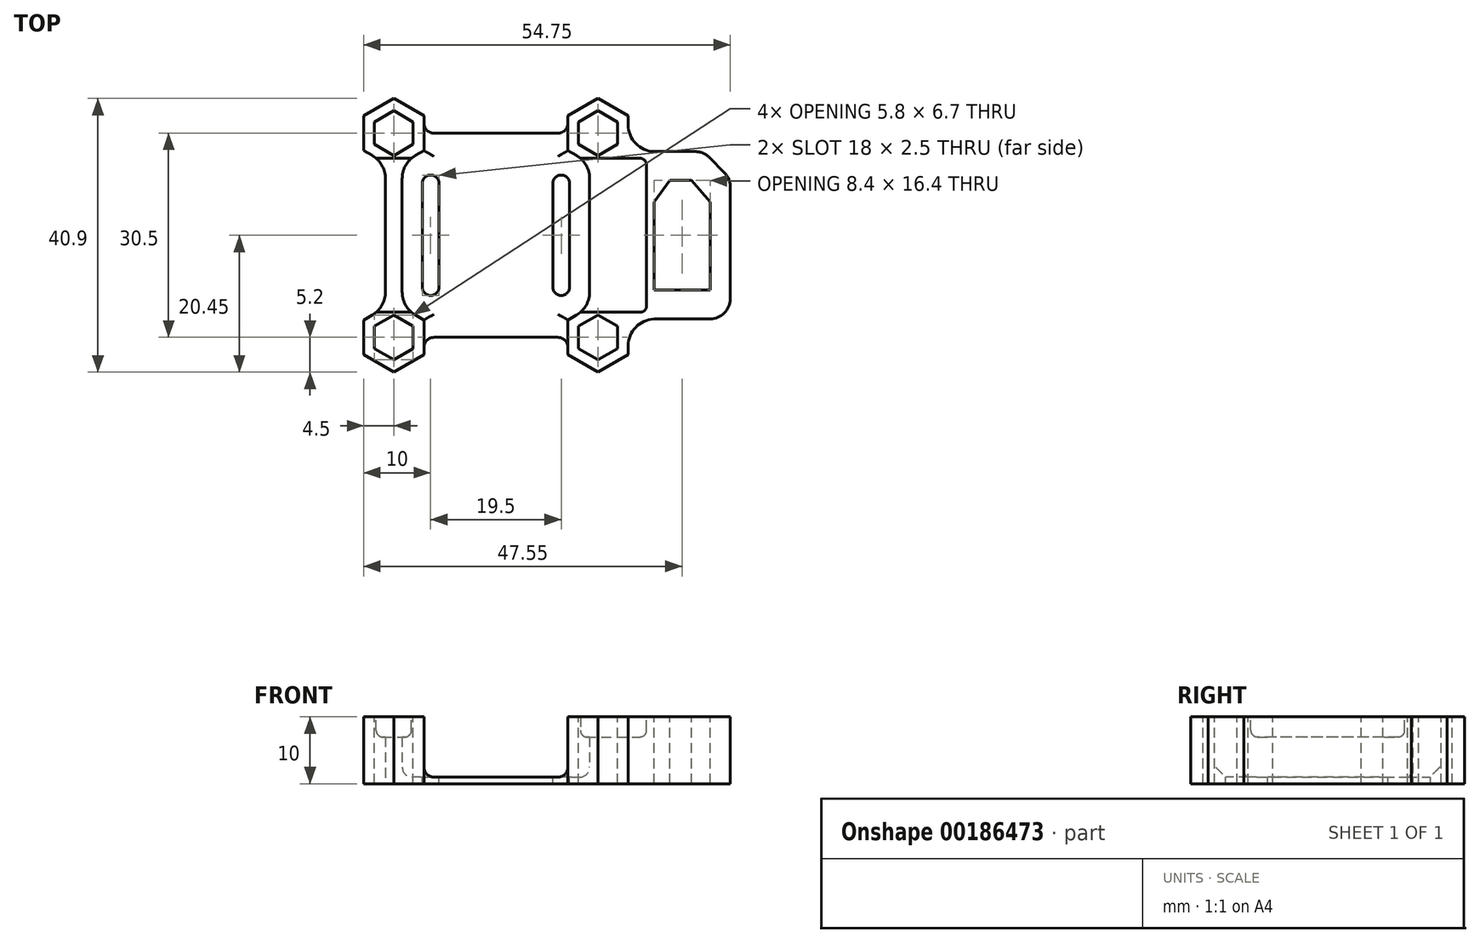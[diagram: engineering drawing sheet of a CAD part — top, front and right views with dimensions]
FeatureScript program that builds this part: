
annotation { "Feature Type Name" : "Feature", "Feature Type Description" : "" }
export const myFeature = defineFeature(function(context is Context, id is Id, definition is map)
    precondition{}
    {
        {
            var Q0;
            Q0=qCreatedBy(makeId("Top.planeOp"),FACE);
            var sketch = newSketch(context, id + "F0", { "sketchPlane" : qUnion([Q0])});
            skLineSegment(sketch, "E0.bottom", {"start": v(-15.25, 15.25) * mm, "end": v(15.25, 15.25) * mm});
            skLineSegment(sketch, "E0.top", {"start": v(-15.25, -15.25) * mm, "end": v(15.25, -15.25) * mm});
            skLineSegment(sketch, "E0.left", {"start": v(-15.25, 15.25) * mm, "end": v(-15.25, -15.25) * mm});
            skLineSegment(sketch, "E0.right", {"start": v(15.25, 15.25) * mm, "end": v(15.25, -15.25) * mm});
            skSolve(sketch);
        }
        {
            var Q0;
            Q0=qSketchRegion(id+"F0",true);
            extrude(context, id + "F1", {"entities" : qUnion([Q0]), "depth" : 1 * mm});
        }
        {
            var Q0;
            Q0=qCreatedBy(makeId("Top.planeOp"),FACE);
            var sketch = newSketch(context, id + "F2", { "sketchPlane" : qUnion([Q0])});
            skCircle(sketch, "E1.cCircle", {"center": v(-15.25, 15.25) * mm, "radius": 4.5 * mm, "construction": true});
            skLineSegment(sketch, "E1.0", {"start": v(-16.5, 10.78) * mm, "end": v(-19.75, 12.65) * mm});
            skLineSegment(sketch, "E1.1", {"start": v(-19.75, 12.65) * mm, "end": v(-19.75, 17.85) * mm});
            skLineSegment(sketch, "E1.2", {"start": v(-19.75, 17.85) * mm, "end": v(-15.25, 20.45) * mm});
            skLineSegment(sketch, "E1.3", {"start": v(-15.25, 20.45) * mm, "end": v(-10.75, 17.85) * mm});
            skLineSegment(sketch, "E1.4", {"start": v(-10.75, 17.85) * mm, "end": v(-10.75, 12.65) * mm});
            skLineSegment(sketch, "E1.5", {"start": v(-10.75, 12.65) * mm, "end": v(-14, 10.78) * mm});
            skPoint(sketch, "E1.0.midPoint", {"position": v(-17.5, 11.35) * mm});
            skCircle(sketch, "E2.MirrorC", {"center": v(15.25, 15.25) * mm, "radius": 4.5 * mm, "construction": true});
            skLineSegment(sketch, "E3.MirrorCS", {"start": v(19.75, 12.65) * mm, "end": v(19.75, 17.85) * mm});
            skLineSegment(sketch, "E4.MirrorCS", {"start": v(19.75, 17.85) * mm, "end": v(15.25, 20.45) * mm});
            skLineSegment(sketch, "E5.MirrorCS", {"start": v(15.25, 20.45) * mm, "end": v(10.75, 17.85) * mm});
            skLineSegment(sketch, "E6.MirrorCS", {"start": v(10.75, 17.85) * mm, "end": v(10.75, 12.65) * mm});
            skLineSegment(sketch, "E7.MirrorCS", {"start": v(10.75, 12.65) * mm, "end": v(14, 10.78) * mm});
            skPoint(sketch, "E8.MirrorP", {"position": v(17.5, 11.35) * mm});
            skLineSegment(sketch, "E9.MirrorCS", {"start": v(-16.5, -10.78) * mm, "end": v(-19.75, -12.65) * mm});
            skLineSegment(sketch, "E10.MirrorCS", {"start": v(-19.75, -12.65) * mm, "end": v(-19.75, -17.85) * mm});
            skLineSegment(sketch, "E11.MirrorCS", {"start": v(10.75, -17.85) * mm, "end": v(10.75, -12.65) * mm});
            skLineSegment(sketch, "E12.MirrorCS", {"start": v(10.75, -12.65) * mm, "end": v(14, -10.78) * mm});
            skLineSegment(sketch, "E13.MirrorCS", {"start": v(-19.75, -17.85) * mm, "end": v(-15.25, -20.45) * mm});
            skLineSegment(sketch, "E14.MirrorCS", {"start": v(15.25, -20.45) * mm, "end": v(10.75, -17.85) * mm});
            skLineSegment(sketch, "E15.MirrorCS", {"start": v(-15.25, -20.45) * mm, "end": v(-10.75, -17.85) * mm});
            skLineSegment(sketch, "E16.MirrorCS", {"start": v(19.75, -17.85) * mm, "end": v(15.25, -20.45) * mm});
            skLineSegment(sketch, "E17.MirrorCS", {"start": v(-10.75, -17.85) * mm, "end": v(-10.75, -12.65) * mm});
            skLineSegment(sketch, "E18.MirrorCS", {"start": v(19.75, -12.65) * mm, "end": v(19.75, -17.85) * mm});
            skCircle(sketch, "E19.MirrorC", {"center": v(-15.25, -15.25) * mm, "radius": 4.5 * mm, "construction": true});
            skCircle(sketch, "E20.MirrorC", {"center": v(15.25, -15.25) * mm, "radius": 4.5 * mm, "construction": true});
            skPoint(sketch, "E21.MirrorP", {"position": v(17.5, -11.35) * mm});
            skLineSegment(sketch, "E22.MirrorCS", {"start": v(-10.75, -12.65) * mm, "end": v(-14, -10.78) * mm});
            skPoint(sketch, "E23.MirrorP", {"position": v(-17.5, -11.35) * mm});
            skLineSegment(sketch, "E24", {"start": v(-16.5, 10.78) * mm, "end": v(-16.5, -10.78) * mm});
            skLineSegment(sketch, "E25", {"start": v(-14, -10.78) * mm, "end": v(-14, 10.78) * mm});
            skLineSegment(sketch, "E26", {"start": v(14, 10.78) * mm, "end": v(14, -10.78) * mm});
            skPoint(sketch, "E27.orphan", {"position": v(-15.25, 10.05) * mm});
            skPoint(sketch, "E28.orphan", {"position": v(-15.25, -10.05) * mm});
            skPoint(sketch, "E29.orphan", {"position": v(15.25, -10.05) * mm});
            skPoint(sketch, "E30.orphan", {"position": v(15.25, 10.05) * mm});
            skLineSegment(sketch, "E31", {"start": v(24, 12.5) * mm, "end": v(24, -12.5) * mm, "construction": true});
            skLineSegment(sketch, "E32", {"start": v(24, -12.5) * mm, "end": v(19.75, -12.65) * mm});
            skLineSegment(sketch, "E33", {"start": v(24, 12.5) * mm, "end": v(19.75, 12.65) * mm});
            skLineSegment(sketch, "E34.bottom", {"start": v(24, 12.5) * mm, "end": v(35, 12.5) * mm});
            skLineSegment(sketch, "E34.top", {"start": v(24, -12.5) * mm, "end": v(35, -12.5) * mm});
            skLineSegment(sketch, "E34.right", {"start": v(35, 12.5) * mm, "end": v(35, -12.5) * mm});
            skSolve(sketch);
        }
        {
            var Q0;
            Q0=qSketchRegion(id+"F2",true);
            extrude(context, id + "F3", {"entities" : qUnion([Q0]), "operationType" : NewBodyOperationType.ADD, "depth" : 10 * mm});
        }
        {
            var Q0;
            Q0=makeQuery(id+"F3.opExtrude","CAP_FACE",FACE,{"disambiguationData":[OSD([sQuery(id+"F2.wireOp",EDGE,"E3.MirrorCS"),sQuery(id+"F2.wireOp",EDGE,"E4.MirrorCS"),sQuery(id+"F2.wireOp",EDGE,"E5.MirrorCS"),sQuery(id+"F2.wireOp",EDGE,"E6.MirrorCS"),sQuery(id+"F2.wireOp",EDGE,"E7.MirrorCS"),sQuery(id+"F2.wireOp",EDGE,"E11.MirrorCS"),sQuery(id+"F2.wireOp",EDGE,"E12.MirrorCS"),sQuery(id+"F2.wireOp",EDGE,"E14.MirrorCS"),sQuery(id+"F2.wireOp",EDGE,"E16.MirrorCS"),sQuery(id+"F2.wireOp",EDGE,"E18.MirrorCS"),sQuery(id+"F2.wireOp",EDGE,"E26"),sQuery(id+"F2.wireOp",EDGE,"E31"),sQuery(id+"F2.wireOp",EDGE,"E32"),sQuery(id+"F2.wireOp",EDGE,"E33")])],"isStart":false});
            var sketch = newSketch(context, id + "F4", { "sketchPlane" : qUnion([Q0])});
            skLineSegment(sketch, "E35.bottom", {"start": v(-22.5, 11.5) * mm, "end": v(22.5, 11.5) * mm});
            skLineSegment(sketch, "E35.top", {"start": v(-22.5, -11.5) * mm, "end": v(22.5, -11.5) * mm});
            skLineSegment(sketch, "E35.left", {"start": v(-22.5, 11.5) * mm, "end": v(-22.5, -11.5) * mm});
            skLineSegment(sketch, "E35.right", {"start": v(22.5, 11.5) * mm, "end": v(22.5, -11.5) * mm});
            skPoint(sketch, "E36.visualSharp", {"position": v(22.5, 11.5) * mm});
            skPoint(sketch, "E37.visualSharp", {"position": v(22.5, -11.5) * mm});
            skSolve(sketch);
        }
        {
            var Q0;
            Q0=qSketchRegion(id+"F4",true);
            extrude(context, id + "F5", {"entities" : qUnion([Q0]), "operationType" : NewBodyOperationType.REMOVE, "oppositeDirection" : true, "depth" : 3 * mm});
        }
        {
            var Q0;
            {var subQ0=sQuery(id+"F2.wireOp",EDGE,"E34.top");var subQ1=sQuery(id+"F2.wireOp",EDGE,"E34.bottom");var subQ2=sQuery(id+"F2.wireOp",EDGE,"E33");var subQ3=sQuery(id+"F2.wireOp",EDGE,"E32");var subQ4=sQuery(id+"F2.wireOp",EDGE,"E34.right");Q0=makeQuery(id+"F5.boolean.opBoolean","SPLIT",FACE,{"disambiguationData":[TD([makeQuery(id+"F3.opExtrude","SWEPT_FACE",FACE,{"disambiguationData":[OSD([subQ3])]})])],"derivedFrom":makeQuery(id+"F3.opExtrude","CAP_FACE",FACE,{"disambiguationData":[OSD([sQuery(id+"F2.wireOp",EDGE,"E3.MirrorCS"),sQuery(id+"F2.wireOp",EDGE,"E4.MirrorCS"),sQuery(id+"F2.wireOp",EDGE,"E5.MirrorCS"),sQuery(id+"F2.wireOp",EDGE,"E6.MirrorCS"),sQuery(id+"F2.wireOp",EDGE,"E7.MirrorCS"),sQuery(id+"F2.wireOp",EDGE,"E11.MirrorCS"),sQuery(id+"F2.wireOp",EDGE,"E12.MirrorCS"),sQuery(id+"F2.wireOp",EDGE,"E14.MirrorCS"),sQuery(id+"F2.wireOp",EDGE,"E16.MirrorCS"),sQuery(id+"F2.wireOp",EDGE,"E18.MirrorCS"),sQuery(id+"F2.wireOp",EDGE,"E26"),subQ3,subQ2,subQ1,subQ0,subQ4])],"isStart":false})});}
            var sketch = newSketch(context, id + "F6", { "sketchPlane" : qUnion([Q0])});
            skLineSegment(sketch, "E38.bottom", {"start": v(26, 8.2) * mm, "end": v(29.2, 8.2) * mm});
            skLineSegment(sketch, "E38.top", {"start": v(23.6, -8.2) * mm, "end": v(32, -8.2) * mm});
            skLineSegment(sketch, "E38.left", {"start": v(23.6, 5) * mm, "end": v(23.6, -8.2) * mm});
            skLineSegment(sketch, "E38.right", {"start": v(32, 5) * mm, "end": v(32, -8.2) * mm});
            skLineSegment(sketch, "E39", {"start": v(26, 8.2) * mm, "end": v(23.6, 5) * mm});
            skLineSegment(sketch, "E40", {"start": v(29.2, 8.2) * mm, "end": v(32, 5) * mm});
            skCircle(sketch, "E41.cCircle", {"center": v(-15.25, 15.25) * mm, "radius": 2.9 * mm, "construction": true});
            skLineSegment(sketch, "E41.0", {"start": v(-12.35, 13.58) * mm, "end": v(-15.25, 11.9) * mm});
            skLineSegment(sketch, "E41.1", {"start": v(-15.25, 11.9) * mm, "end": v(-18.15, 13.58) * mm});
            skLineSegment(sketch, "E41.2", {"start": v(-18.15, 13.58) * mm, "end": v(-18.15, 16.92) * mm});
            skLineSegment(sketch, "E41.3", {"start": v(-18.15, 16.92) * mm, "end": v(-15.25, 18.6) * mm});
            skLineSegment(sketch, "E41.4", {"start": v(-15.25, 18.6) * mm, "end": v(-12.35, 16.92) * mm});
            skLineSegment(sketch, "E41.5", {"start": v(-12.35, 16.92) * mm, "end": v(-12.35, 13.58) * mm});
            skPoint(sketch, "E41.0.midPoint", {"position": v(-13.8, 12.74) * mm});
            skLineSegment(sketch, "E42.0.1.0", {"start": v(-15.25, -11.9) * mm, "end": v(-12.35, -13.58) * mm});
            skLineSegment(sketch, "E42.0.1.1", {"start": v(-15.25, -18.6) * mm, "end": v(-18.15, -16.92) * mm});
            skLineSegment(sketch, "E42.0.1.2", {"start": v(-18.15, -13.58) * mm, "end": v(-15.25, -11.9) * mm});
            skPoint(sketch, "E42.0.1.3", {"position": v(-13.8, -17.76) * mm});
            skCircle(sketch, "E42.0.1.4", {"center": v(-15.25, -15.25) * mm, "radius": 2.9 * mm, "construction": true});
            skLineSegment(sketch, "E42.0.1.5", {"start": v(-12.35, -13.58) * mm, "end": v(-12.35, -16.92) * mm});
            skLineSegment(sketch, "E42.0.1.6", {"start": v(-18.15, -16.92) * mm, "end": v(-18.15, -13.58) * mm});
            skLineSegment(sketch, "E42.0.1.7", {"start": v(-12.35, -16.92) * mm, "end": v(-15.25, -18.6) * mm});
            skLineSegment(sketch, "E42.direction1", {"start": v(-18.15, 13.58) * mm, "end": v(12.35, 13.58) * mm, "construction": true});
            skLineSegment(sketch, "E42.direction2", {"start": v(-18.15, 13.58) * mm, "end": v(-18.15, -16.92) * mm, "construction": true});
            skLineSegment(sketch, "E43.MirrorCS", {"start": v(12.35, 16.92) * mm, "end": v(12.35, 13.58) * mm});
            skLineSegment(sketch, "E44.MirrorCS", {"start": v(18.15, 16.92) * mm, "end": v(15.25, 18.6) * mm});
            skLineSegment(sketch, "E45.MirrorCS", {"start": v(12.35, -16.92) * mm, "end": v(15.25, -18.6) * mm});
            skLineSegment(sketch, "E46.MirrorCS", {"start": v(18.15, 13.58) * mm, "end": v(18.15, 16.92) * mm});
            skLineSegment(sketch, "E47.MirrorCS", {"start": v(15.25, 11.9) * mm, "end": v(18.15, 13.58) * mm});
            skLineSegment(sketch, "E48.MirrorCS", {"start": v(12.35, 13.58) * mm, "end": v(15.25, 11.9) * mm});
            skLineSegment(sketch, "E49.MirrorCS", {"start": v(18.15, -13.58) * mm, "end": v(15.25, -11.9) * mm});
            skLineSegment(sketch, "E50.MirrorCS", {"start": v(15.25, -11.9) * mm, "end": v(12.35, -13.58) * mm});
            skLineSegment(sketch, "E51.MirrorCS", {"start": v(12.35, -13.58) * mm, "end": v(12.35, -16.92) * mm});
            skLineSegment(sketch, "E52.MirrorCS", {"start": v(18.15, -16.92) * mm, "end": v(18.15, -13.58) * mm});
            skLineSegment(sketch, "E53.MirrorCS", {"start": v(15.25, 18.6) * mm, "end": v(12.35, 16.92) * mm});
            skCircle(sketch, "E54.MirrorC", {"center": v(15.25, -15.25) * mm, "radius": 2.9 * mm, "construction": true});
            skLineSegment(sketch, "E55.MirrorCS", {"start": v(15.25, -18.6) * mm, "end": v(18.15, -16.92) * mm});
            skPoint(sketch, "E56.MirrorP", {"position": v(13.8, -17.76) * mm});
            skLineSegment(sketch, "E57.MirrorCS", {"start": v(18.15, 13.58) * mm, "end": v(18.15, -16.92) * mm, "construction": true});
            skPoint(sketch, "E58.MirrorP", {"position": v(13.8, 12.74) * mm});
            skCircle(sketch, "E59.MirrorC", {"center": v(15.25, 15.25) * mm, "radius": 2.9 * mm, "construction": true});
            skSolve(sketch);
        }
        {
            var Q0;
            Q0=qSketchRegion(id+"F6",true);
            extrude(context, id + "F7", {"entities" : qUnion([Q0]), "operationType" : NewBodyOperationType.REMOVE, "endBound" : BoundingType.THROUGH_ALL, "oppositeDirection" : true, "depth" : 25 * mm});
        }
        {
            var Q0;
            Q0=makeQuery(id+"F3.opExtrude","SWEPT_EDGE",EDGE,{"disambiguationData":[OSD([sQuery(id+"F2.wireOp",EDGE,"E34.bottom"),sQuery(id+"F2.wireOp",EDGE,"E34.right")])]});
            chamfer(context, id + "F8", {"entities" : qUnion([Q0]), "width" : 4 * mm, "tangentPropagation" : true});
        }
        {
            var Q0;
            Q0=makeQuery(id+"F3.opExtrude","SWEPT_EDGE",EDGE,{"disambiguationData":[OSD([sQuery(id+"F2.wireOp",EDGE,"E1.0"),sQuery(id+"F2.wireOp",EDGE,"E24")])]});
            var Q1;
            Q1=makeQuery(id+"F3.opExtrude","SWEPT_EDGE",EDGE,{"disambiguationData":[OSD([sQuery(id+"F2.wireOp",EDGE,"E9.MirrorCS"),sQuery(id+"F2.wireOp",EDGE,"E24")])]});
            var Q2;
            Q2=makeQuery(id+"F3.opExtrude","SWEPT_EDGE",EDGE,{"disambiguationData":[OSD([sQuery(id+"F2.wireOp",EDGE,"E1.5"),sQuery(id+"F2.wireOp",EDGE,"E25")])]});
            var Q3;
            Q3=makeQuery(id+"F3.opExtrude","SWEPT_EDGE",EDGE,{"disambiguationData":[OSD([sQuery(id+"F2.wireOp",EDGE,"E22.MirrorCS"),sQuery(id+"F2.wireOp",EDGE,"E25")])]});
            var Q4;
            Q4=makeQuery(id+"F3.opExtrude","SWEPT_EDGE",EDGE,{"disambiguationData":[OSD([sQuery(id+"F2.wireOp",EDGE,"E7.MirrorCS"),sQuery(id+"F2.wireOp",EDGE,"E26")])]});
            var Q5;
            Q5=makeQuery(id+"F3.opExtrude","SWEPT_EDGE",EDGE,{"disambiguationData":[OSD([sQuery(id+"F2.wireOp",EDGE,"E12.MirrorCS"),sQuery(id+"F2.wireOp",EDGE,"E26")])]});
            var Q6;
            Q6=makeQuery(id+"F3.opExtrude","SWEPT_EDGE",EDGE,{"disambiguationData":[OSD([sQuery(id+"F2.wireOp",EDGE,"E33"),sQuery(id+"F2.wireOp",EDGE,"E34.bottom")])]});
            var Q7;
            Q7=makeQuery(id+"F3.opExtrude","SWEPT_EDGE",EDGE,{"disambiguationData":[OSD([sQuery(id+"F2.wireOp",EDGE,"E3.MirrorCS"),sQuery(id+"F2.wireOp",EDGE,"E33")])]});
            var Q8;
            Q8=makeQuery(id+"F3.opExtrude","SWEPT_EDGE",EDGE,{"disambiguationData":[OSD([sQuery(id+"F2.wireOp",EDGE,"E18.MirrorCS"),sQuery(id+"F2.wireOp",EDGE,"E32")])]});
            var Q9;
            Q9=makeQuery(id+"F3.opExtrude","SWEPT_EDGE",EDGE,{"disambiguationData":[OSD([sQuery(id+"F2.wireOp",EDGE,"E32"),sQuery(id+"F2.wireOp",EDGE,"E34.top")])]});
            fillet(context, id + "F9", {"entities" : qUnion([Q0, Q1, Q2, Q3, Q4, Q5, Q6, Q7, Q8, Q9]), "radius" : 4 * mm, "tangentPropagation" : true, "allowEdgeOverflow" : false});
        }
        {
            var Q0;
            {var subQ0=sQuery(id+"F4.wireOp",EDGE,"E35.top");Q0=makeQuery(id+"F5.boolean.opBoolean","COPY",EDGE,{"disambiguationData":[TD([makeQuery(id+"F3.opExtrude","SWEPT_FACE",FACE,{"disambiguationData":[OSD([sQuery(id+"F2.wireOp",EDGE,"E9.MirrorCS")])]})])],"derivedFrom":makeQuery(id+"F5.opExtrude","CAP_EDGE",EDGE,{"disambiguationData":[OSD([subQ0])],"isStart":false})});}
            var Q1;
            {var subQ0=sQuery(id+"F4.wireOp",EDGE,"E35.bottom");Q1=makeQuery(id+"F5.boolean.opBoolean","COPY",EDGE,{"disambiguationData":[TD([makeQuery(id+"F3.opExtrude","SWEPT_FACE",FACE,{"disambiguationData":[OSD([sQuery(id+"F2.wireOp",EDGE,"E1.0")])]})])],"derivedFrom":makeQuery(id+"F5.opExtrude","CAP_EDGE",EDGE,{"disambiguationData":[OSD([subQ0])],"isStart":false})});}
            var Q2;
            {var subQ1=sQuery(id+"F4.wireOp",EDGE,"E35.bottom");Q2=makeQuery(id+"F5.boolean.opBoolean","COPY",EDGE,{"disambiguationData":[TD([makeQuery(id+"F3.opExtrude","SWEPT_FACE",FACE,{"disambiguationData":[OSD([sQuery(id+"F2.wireOp",EDGE,"E3.MirrorCS")])]})])],"derivedFrom":makeQuery(id+"F5.opExtrude","CAP_EDGE",EDGE,{"disambiguationData":[OSD([subQ1])],"isStart":false})});}
            var Q3;
            {var subQ0=sQuery(id+"F4.wireOp",EDGE,"E35.top");Q3=makeQuery(id+"F5.boolean.opBoolean","COPY",EDGE,{"disambiguationData":[TD([makeQuery(id+"F3.opExtrude","SWEPT_FACE",FACE,{"disambiguationData":[OSD([sQuery(id+"F2.wireOp",EDGE,"E12.MirrorCS")])]})])],"derivedFrom":makeQuery(id+"F5.opExtrude","CAP_EDGE",EDGE,{"disambiguationData":[OSD([subQ0])],"isStart":false})});}
            var Q4;
            Q4=makeQuery(id+"F5.boolean.opBoolean","COPY",EDGE,{"derivedFrom":makeQuery(id+"F5.opExtrude","CAP_EDGE",EDGE,{"disambiguationData":[OSD([sQuery(id+"F4.wireOp",EDGE,"E35.right")])],"isStart":false})});
            var Q5;
            {var subQ0=sQuery(id+"F4.wireOp",EDGE,"E35.bottom");Q5=makeQuery(id+"F5.boolean.opBoolean","COPY",EDGE,{"disambiguationData":[TD([makeQuery(id+"F3.opExtrude","SWEPT_FACE",FACE,{"disambiguationData":[OSD([sQuery(id+"F2.wireOp",EDGE,"E7.MirrorCS")])]})])],"derivedFrom":makeQuery(id+"F5.opExtrude","CAP_EDGE",EDGE,{"disambiguationData":[OSD([subQ0])],"isStart":false})});}
            fillet(context, id + "F10", {"entities" : qUnion([Q0, Q1, Q2, Q3, Q4, Q5]), "radius" : 1 * mm, "tangentPropagation" : true, "allowEdgeOverflow" : false});
        }
        {
            var Q0;
            Q0=makeQuery(id+"F9.opFillet","BLEND_EDGE",EDGE,{"blendedFrom":[makeQuery(id+"F3.opExtrude","SWEPT_EDGE",EDGE,{"disambiguationData":[OSD([sQuery(id+"F2.wireOp",EDGE,"E22.MirrorCS"),sQuery(id+"F2.wireOp",EDGE,"E25")])]}),makeQuery(id+"F1.opExtrude","CAP_FACE",FACE,{"disambiguationData":[OSD([sQuery(id+"F0.wireOp",EDGE,"E0.bottom"),sQuery(id+"F0.wireOp",EDGE,"E0.top"),sQuery(id+"F0.wireOp",EDGE,"E0.left"),sQuery(id+"F0.wireOp",EDGE,"E0.right")])],"isStart":false})],"blendedInto":[makeQuery(id+"F1.opExtrude","CAP_FACE",FACE,{"disambiguationData":[OSD([sQuery(id+"F0.wireOp",EDGE,"E0.bottom"),sQuery(id+"F0.wireOp",EDGE,"E0.top"),sQuery(id+"F0.wireOp",EDGE,"E0.left"),sQuery(id+"F0.wireOp",EDGE,"E0.right")])],"isStart":false})]});
            var Q1;
            Q1=makeQuery(id+"F3.boolean.opBoolean","INTERSECT",EDGE,{"derivedFrom":[makeQuery(id+"F1.opExtrude","CAP_FACE",FACE,{"disambiguationData":[OSD([sQuery(id+"F0.wireOp",EDGE,"E0.bottom"),sQuery(id+"F0.wireOp",EDGE,"E0.top"),sQuery(id+"F0.wireOp",EDGE,"E0.left"),sQuery(id+"F0.wireOp",EDGE,"E0.right")])],"isStart":false}),makeQuery(id+"F3.opExtrude","SWEPT_FACE",FACE,{"disambiguationData":[OSD([sQuery(id+"F2.wireOp",EDGE,"E17.MirrorCS")])]})]});
            var Q2;
            Q2=makeQuery(id+"F3.boolean.opBoolean","INTERSECT",EDGE,{"derivedFrom":[makeQuery(id+"F1.opExtrude","CAP_FACE",FACE,{"disambiguationData":[OSD([sQuery(id+"F0.wireOp",EDGE,"E0.bottom"),sQuery(id+"F0.wireOp",EDGE,"E0.top"),sQuery(id+"F0.wireOp",EDGE,"E0.left"),sQuery(id+"F0.wireOp",EDGE,"E0.right")])],"isStart":false}),makeQuery(id+"F3.opExtrude","SWEPT_FACE",FACE,{"disambiguationData":[OSD([sQuery(id+"F2.wireOp",EDGE,"E1.4")])]})]});
            var Q3;
            Q3=makeQuery(id+"F3.boolean.opBoolean","INTERSECT",EDGE,{"derivedFrom":[makeQuery(id+"F1.opExtrude","CAP_FACE",FACE,{"disambiguationData":[OSD([sQuery(id+"F0.wireOp",EDGE,"E0.bottom"),sQuery(id+"F0.wireOp",EDGE,"E0.top"),sQuery(id+"F0.wireOp",EDGE,"E0.left"),sQuery(id+"F0.wireOp",EDGE,"E0.right")])],"isStart":false}),makeQuery(id+"F3.opExtrude","SWEPT_FACE",FACE,{"disambiguationData":[OSD([sQuery(id+"F2.wireOp",EDGE,"E26")])]})]});
            var Q4;
            Q4=makeQuery(id+"F3.boolean.opBoolean","INTERSECT",EDGE,{"derivedFrom":[makeQuery(id+"F1.opExtrude","CAP_FACE",FACE,{"disambiguationData":[OSD([sQuery(id+"F0.wireOp",EDGE,"E0.bottom"),sQuery(id+"F0.wireOp",EDGE,"E0.top"),sQuery(id+"F0.wireOp",EDGE,"E0.left"),sQuery(id+"F0.wireOp",EDGE,"E0.right")])],"isStart":false}),makeQuery(id+"F3.opExtrude","SWEPT_FACE",FACE,{"disambiguationData":[OSD([sQuery(id+"F2.wireOp",EDGE,"E6.MirrorCS")])]})]});
            var Q5;
            Q5=makeQuery(id+"F3.boolean.opBoolean","INTERSECT",EDGE,{"derivedFrom":[makeQuery(id+"F1.opExtrude","CAP_FACE",FACE,{"disambiguationData":[OSD([sQuery(id+"F0.wireOp",EDGE,"E0.bottom"),sQuery(id+"F0.wireOp",EDGE,"E0.top"),sQuery(id+"F0.wireOp",EDGE,"E0.left"),sQuery(id+"F0.wireOp",EDGE,"E0.right")])],"isStart":false}),makeQuery(id+"F3.opExtrude","SWEPT_FACE",FACE,{"disambiguationData":[OSD([sQuery(id+"F2.wireOp",EDGE,"E11.MirrorCS")])]})]});
            fillet(context, id + "F11", {"entities" : qUnion([Q0, Q1, Q2, Q3, Q4, Q5]), "radius" : 1.5 * mm, "tangentPropagation" : true, "allowEdgeOverflow" : false});
        }
        {
            var Q0;
            Q0=makeQuery(id+"F5.boolean.opBoolean","COPY",EDGE,{"derivedFrom":makeQuery(id+"F5.opExtrude","SWEPT_EDGE",EDGE,{"disambiguationData":[OSD([sQuery(id+"F4.wireOp",EDGE,"E35.bottom"),sQuery(id+"F4.wireOp",EDGE,"E35.right")])]})});
            var Q1;
            Q1=makeQuery(id+"F5.boolean.opBoolean","COPY",EDGE,{"derivedFrom":makeQuery(id+"F5.opExtrude","SWEPT_EDGE",EDGE,{"disambiguationData":[OSD([sQuery(id+"F4.wireOp",EDGE,"E35.top"),sQuery(id+"F4.wireOp",EDGE,"E35.right")])]})});
            fillet(context, id + "F12", {"entities" : qUnion([Q0, Q1]), "radius" : 1 * mm, "tangentPropagation" : true, "allowEdgeOverflow" : false});
        }
        {
            var Q0;
            Q0=makeQuery(id+"F3.opExtrude","SWEPT_EDGE",EDGE,{"disambiguationData":[OSD([sQuery(id+"F2.wireOp",EDGE,"E34.top"),sQuery(id+"F2.wireOp",EDGE,"E34.right")])]});
            var Q1;
            {var subQ0=sQuery(id+"F2.wireOp",EDGE,"E34.right");Q1=makeQuery(id+"F8.opChamfer","BLEND_EDGE",EDGE,{"blendedFrom":[makeQuery(id+"F3.opExtrude","SWEPT_EDGE",EDGE,{"disambiguationData":[OSD([sQuery(id+"F2.wireOp",EDGE,"E34.bottom"),subQ0])]}),makeQuery(id+"F3.opExtrude","SWEPT_FACE",FACE,{"disambiguationData":[OSD([subQ0])]})],"blendedInto":[makeQuery(id+"F3.opExtrude","SWEPT_FACE",FACE,{"disambiguationData":[OSD([subQ0])]})]});}
            var Q2;
            {var subQ0=sQuery(id+"F2.wireOp",EDGE,"E34.bottom");Q2=makeQuery(id+"F8.opChamfer","BLEND_EDGE",EDGE,{"blendedFrom":[makeQuery(id+"F3.opExtrude","SWEPT_EDGE",EDGE,{"disambiguationData":[OSD([subQ0,sQuery(id+"F2.wireOp",EDGE,"E34.right")])]}),makeQuery(id+"F3.opExtrude","SWEPT_FACE",FACE,{"disambiguationData":[OSD([subQ0])]})],"blendedInto":[makeQuery(id+"F3.opExtrude","SWEPT_FACE",FACE,{"disambiguationData":[OSD([subQ0])]})]});}
            fillet(context, id + "F13", {"entities" : qUnion([Q0, Q1, Q2]), "radius" : 3 * mm, "tangentPropagation" : true, "allowEdgeOverflow" : false});
        }
        {
            var Q0;
            Q0=makeQuery(id+"F3.boolean.opBoolean","INTERSECT",EDGE,{"derivedFrom":[makeQuery(id+"F1.opExtrude","SWEPT_FACE",FACE,{"disambiguationData":[OSD([sQuery(id+"F0.wireOp",EDGE,"E0.bottom")])]}),makeQuery(id+"F3.opExtrude","SWEPT_FACE",FACE,{"disambiguationData":[OSD([sQuery(id+"F2.wireOp",EDGE,"E6.MirrorCS")])]})]});
            var Q1;
            Q1=makeQuery(id+"F3.boolean.opBoolean","INTERSECT",EDGE,{"derivedFrom":[makeQuery(id+"F1.opExtrude","SWEPT_FACE",FACE,{"disambiguationData":[OSD([sQuery(id+"F0.wireOp",EDGE,"E0.bottom")])]}),makeQuery(id+"F3.opExtrude","SWEPT_FACE",FACE,{"disambiguationData":[OSD([sQuery(id+"F2.wireOp",EDGE,"E1.4")])]})]});
            var Q2;
            Q2=makeQuery(id+"F3.boolean.opBoolean","INTERSECT",EDGE,{"derivedFrom":[makeQuery(id+"F1.opExtrude","SWEPT_FACE",FACE,{"disambiguationData":[OSD([sQuery(id+"F0.wireOp",EDGE,"E0.top")])]}),makeQuery(id+"F3.opExtrude","SWEPT_FACE",FACE,{"disambiguationData":[OSD([sQuery(id+"F2.wireOp",EDGE,"E17.MirrorCS")])]})]});
            var Q3;
            Q3=makeQuery(id+"F3.boolean.opBoolean","INTERSECT",EDGE,{"derivedFrom":[makeQuery(id+"F1.opExtrude","SWEPT_FACE",FACE,{"disambiguationData":[OSD([sQuery(id+"F0.wireOp",EDGE,"E0.top")])]}),makeQuery(id+"F3.opExtrude","SWEPT_FACE",FACE,{"disambiguationData":[OSD([sQuery(id+"F2.wireOp",EDGE,"E11.MirrorCS")])]})]});
            fillet(context, id + "F14", {"entities" : qUnion([Q0, Q1, Q2, Q3]), "radius" : 1.5 * mm, "tangentPropagation" : true, "allowEdgeOverflow" : false});
        }
        {
            var Q0;
            Q0=makeQuery(id+"F1.opExtrude","CAP_FACE",FACE,{"disambiguationData":[OSD([sQuery(id+"F0.wireOp",EDGE,"E0.bottom"),sQuery(id+"F0.wireOp",EDGE,"E0.top"),sQuery(id+"F0.wireOp",EDGE,"E0.left"),sQuery(id+"F0.wireOp",EDGE,"E0.right")])],"isStart":false});
            var sketch = newSketch(context, id + "F15", { "sketchPlane" : qUnion([Q0])});
            skLineSegment(sketch, "E60.bottom", {"start": v(-9.75, 9) * mm, "end": v(-9.75, 9) * mm});
            skLineSegment(sketch, "E60.top", {"start": v(-9.75, -9) * mm, "end": v(-9.75, -9) * mm});
            skLineSegment(sketch, "E60.left", {"start": v(-11, 7.75) * mm, "end": v(-11, -7.75) * mm});
            skLineSegment(sketch, "E60.right", {"start": v(-8.5, 7.75) * mm, "end": v(-8.5, -7.75) * mm});
            skPoint(sketch, "E61.visualSharp", {"position": v(-11, 9) * mm});
            skArc(sketch, "E61.filletArc", {"start": v(-9.75, 9) * mm, "mid": v(-10.63, 8.63) * mm, "end": v(-11, 7.75) * mm});
            skPoint(sketch, "E62.visualSharp", {"position": v(-8.5, 9) * mm});
            skArc(sketch, "E62.filletArc", {"start": v(-8.5, 7.75) * mm, "mid": v(-8.87, 8.63) * mm, "end": v(-9.75, 9) * mm});
            skPoint(sketch, "E63.visualSharp", {"position": v(-11, -9) * mm});
            skArc(sketch, "E63.filletArc", {"start": v(-11, -7.75) * mm, "mid": v(-10.63, -8.63) * mm, "end": v(-9.75, -9) * mm});
            skPoint(sketch, "E64.visualSharp", {"position": v(-8.5, -9) * mm});
            skArc(sketch, "E64.filletArc", {"start": v(-9.75, -9) * mm, "mid": v(-8.87, -8.63) * mm, "end": v(-8.5, -7.75) * mm});
            skArc(sketch, "E65.MirrorCS", {"start": v(9.75, -9) * mm, "mid": v(8.87, -8.63) * mm, "end": v(8.5, -7.75) * mm});
            skArc(sketch, "E66.MirrorCS", {"start": v(11, -7.75) * mm, "mid": v(10.63, -8.63) * mm, "end": v(9.75, -9) * mm});
            skArc(sketch, "E67.MirrorCS", {"start": v(8.5, 7.75) * mm, "mid": v(8.87, 8.63) * mm, "end": v(9.75, 9) * mm});
            skArc(sketch, "E68.MirrorCS", {"start": v(9.75, 9) * mm, "mid": v(10.63, 8.63) * mm, "end": v(11, 7.75) * mm});
            skPoint(sketch, "E69.MirrorP", {"position": v(11, -9) * mm});
            skPoint(sketch, "E70.MirrorP", {"position": v(8.5, -9) * mm});
            skPoint(sketch, "E71.MirrorP", {"position": v(11, 9) * mm});
            skPoint(sketch, "E72.MirrorP", {"position": v(8.5, 9) * mm});
            skLineSegment(sketch, "E73.MirrorCS", {"start": v(9.75, -9) * mm, "end": v(9.75, -9) * mm});
            skLineSegment(sketch, "E74.MirrorCS", {"start": v(9.75, 9) * mm, "end": v(9.75, 9) * mm});
            skLineSegment(sketch, "E75.MirrorCS", {"start": v(11, 7.75) * mm, "end": v(11, -7.75) * mm});
            skLineSegment(sketch, "E76.MirrorCS", {"start": v(8.5, 7.75) * mm, "end": v(8.5, -7.75) * mm});
            skSolve(sketch);
        }
        {
            var Q0;
            Q0 = qSketchRegion(id + "F15", true);
            extrude(context, id + "F16", {"entities" : qUnion([Q0]), "operationType" : NewBodyOperationType.REMOVE, "endBound" : BoundingType.THROUGH_ALL, "oppositeDirection" : true, "depth" : 25 * mm});
        }
    });
